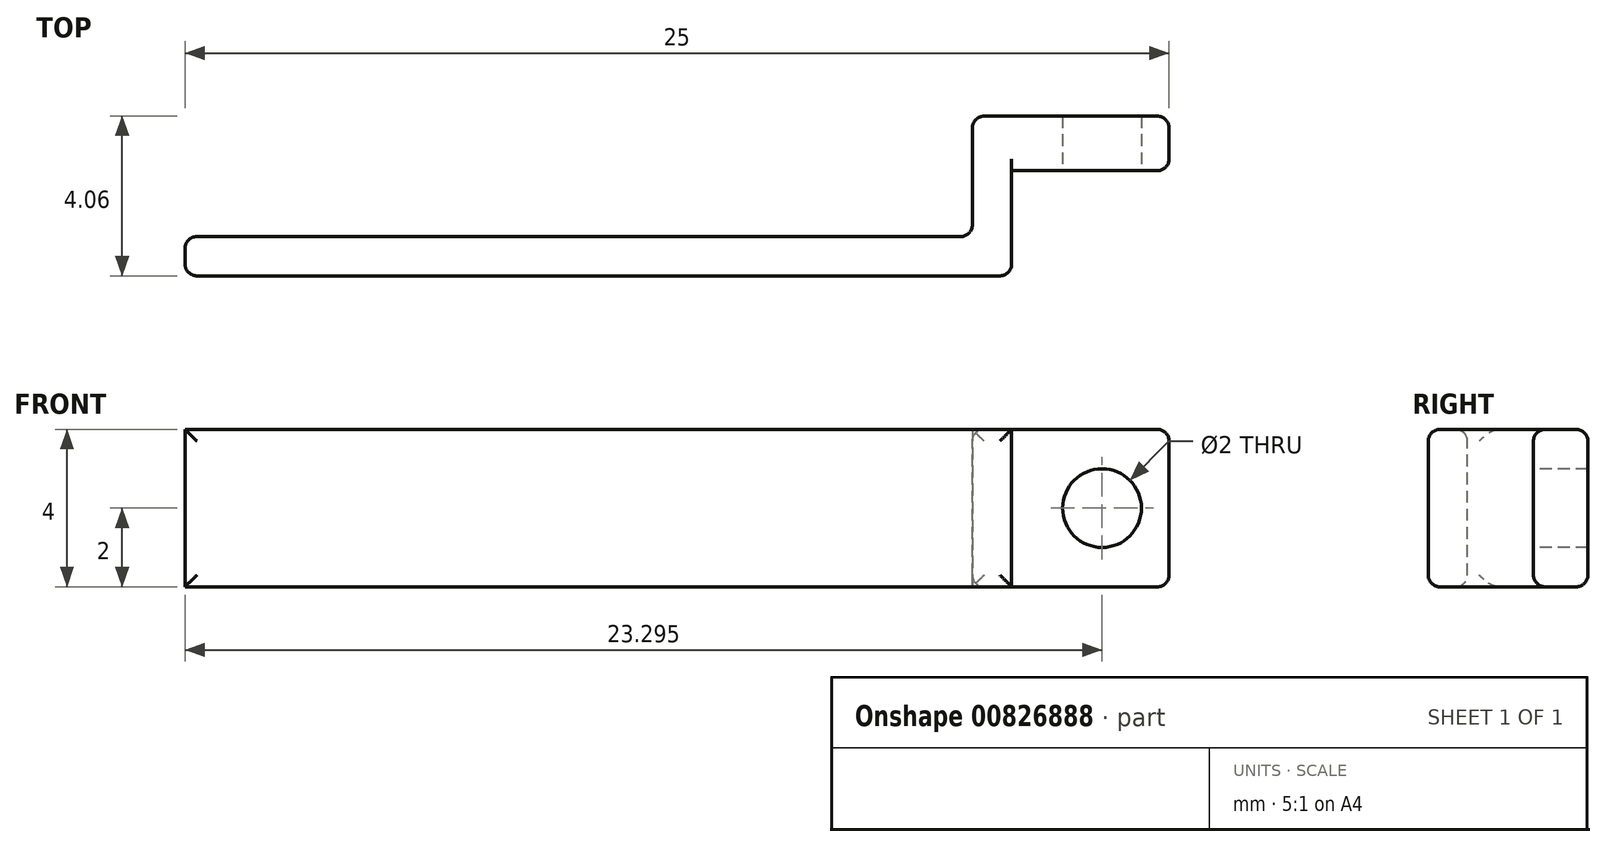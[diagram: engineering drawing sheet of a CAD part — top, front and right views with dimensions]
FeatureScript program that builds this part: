
annotation { "Feature Type Name" : "Feature", "Feature Type Description" : "" }
export const myFeature = defineFeature(function(context is Context, id is Id, definition is map)
    precondition{}
    {
        {
            var Q0;
            Q0=qCreatedBy(makeId("Front.planeOp"),FACE);
            var sketch = newSketch(context, id + "F0", { "sketchPlane" : qUnion([Q0])});
            skLineSegment(sketch, "E0.bottom", {"start": v(0, 0) * mm, "end": v(-20, 0) * mm});
            skLineSegment(sketch, "E0.top", {"start": v(0, 4) * mm, "end": v(-20, 4) * mm});
            skLineSegment(sketch, "E0.left", {"start": v(0, 0) * mm, "end": v(0, 4) * mm});
            skLineSegment(sketch, "E0.right", {"start": v(-20, 0) * mm, "end": v(-20, 4) * mm});
            skSolve(sketch);
        }
        {
            var Q0;
            Q0=makeQuery(id+"F0.imprint","IMPRINT",FACE,{"disambiguationData":[TD([[makeQuery(id+"F0.imprint","IMPRINT",EDGE,{"derivedFrom":sQuery(id+"F0.wireOp",EDGE,"E0.bottom")}),-1.0]])]});
            extrude(context, id + "F1", {"entities" : qUnion([Q0]), "depth" : 1 * mm, "offsetDistance" : 25 * mm});
        }
        {
            var Q0;
            Q0=makeQuery(id+"F1.opExtrude","SWEPT_FACE",FACE,{"disambiguationData":[OSD([sQuery(id+"F0.wireOp",EDGE,"E0.left")])]});
            var sketch = newSketch(context, id + "F2", { "sketchPlane" : qUnion([Q0])});
            skLineSegment(sketch, "E1.bottom", {"start": v(-1, 4) * mm, "end": v(3.06, 4) * mm});
            skLineSegment(sketch, "E1.top", {"start": v(-1, 0) * mm, "end": v(3.06, 0) * mm});
            skLineSegment(sketch, "E1.left", {"start": v(-1, 4) * mm, "end": v(-1, 0) * mm});
            skLineSegment(sketch, "E1.right", {"start": v(3.06, 4) * mm, "end": v(3.06, 0) * mm});
            skSolve(sketch);
        }
        {
            var Q0;
            {var subQ2=sQuery(id+"F2.wireOp",EDGE,"E1.right");Q0=makeQuery(id+"F2.imprint","IMPRINT",FACE,{"disambiguationData":[TD([[makeQuery(id+"F2.imprint","IMPRINT",EDGE,{"derivedFrom":subQ2}),-1.0]])]});}
            var Q1;
            {var subQ2=sQuery(id+"F2.wireOp",EDGE,"E1.left");Q1=makeQuery(id+"F2.imprint","IMPRINT",FACE,{"disambiguationData":[TD([[makeQuery(id+"F2.imprint","IMPRINT",EDGE,{"derivedFrom":subQ2}),-1.0]])]});}
            extrude(context, id + "F3", {"entities" : qUnion([Q0, Q1]), "operationType" : NewBodyOperationType.ADD, "depth" : 1 * mm, "offsetDistance" : 25 * mm});
        }
        {
            var Q0;
            Q0=makeQuery(id+"F3.opExtrude","CAP_FACE",FACE,{"disambiguationData":[OSD([sQuery(id+"F2.wireOp",EDGE,"E1.bottom"),sQuery(id+"F2.wireOp",EDGE,"E1.top"),sQuery(id+"F2.wireOp",EDGE,"E1.left"),sQuery(id+"F2.wireOp",EDGE,"E1.right")])],"isStart":false});
            var sketch = newSketch(context, id + "F4", { "sketchPlane" : qUnion([Q0])});
            skLineSegment(sketch, "E2.bottom", {"start": v(3.06, 4) * mm, "end": v(1.67, 4) * mm});
            skLineSegment(sketch, "E2.top", {"start": v(3.06, 0) * mm, "end": v(1.67, 0) * mm});
            skLineSegment(sketch, "E2.left", {"start": v(3.06, 4) * mm, "end": v(3.06, 0) * mm});
            skLineSegment(sketch, "E2.right", {"start": v(1.67, 4) * mm, "end": v(1.67, 0) * mm});
            skSolve(sketch);
        }
        {
            var Q0;
            Q0=makeQuery(id+"F4.imprint","IMPRINT",FACE,{"disambiguationData":[TD([[makeQuery(id+"F4.imprint","IMPRINT",EDGE,{"derivedFrom":sQuery(id+"F4.wireOp",EDGE,"E2.bottom")}),-1.0]])]});
            extrude(context, id + "F5", {"entities" : qUnion([Q0]), "operationType" : NewBodyOperationType.ADD, "depth" : 4 * mm, "offsetDistance" : 25 * mm});
        }
        {
            var Q0;
            Q0=makeQuery(id+"F5.opExtrude","SWEPT_FACE",FACE,{"disambiguationData":[OSD([sQuery(id+"F4.wireOp",EDGE,"E2.right")])]});
            var sketch = newSketch(context, id + "F6", { "sketchPlane" : qUnion([Q0])});
            skCircle(sketch, "E3", {"center": v(3.3, 2) * mm, "radius": 1 * mm});
            skPoint(sketch, "E3.centerSnap0", {"position": v(1, 2) * mm});
            skSolve(sketch);
        }
        {
            var Q0;
            Q0=makeQuery(id+"F6.imprint","IMPRINT",FACE,{"disambiguationData":[TD([[makeQuery(id+"F6.imprint","IMPRINT",EDGE,{"derivedFrom":sQuery(id+"F6.wireOp",EDGE,"E3")}),1.0]])]});
            extrude(context, id + "F7", {"entities" : qUnion([Q0]), "operationType" : NewBodyOperationType.REMOVE, "oppositeDirection" : true, "depth" : 2 * mm, "offsetDistance" : 25 * mm});
        }
        {
            var Q0;
            Q0=makeQuery(id+"F3.boolean.opBoolean","MERGE",FACE,{"derivedFrom":[makeQuery(id+"F1.opExtrude","CAP_FACE",FACE,{"disambiguationData":[OSD([sQuery(id+"F0.wireOp",EDGE,"E0.bottom"),sQuery(id+"F0.wireOp",EDGE,"E0.top"),sQuery(id+"F0.wireOp",EDGE,"E0.left"),sQuery(id+"F0.wireOp",EDGE,"E0.right")])],"isStart":false}),makeQuery(id+"F3.opExtrude","SWEPT_FACE",FACE,{"disambiguationData":[OSD([sQuery(id+"F2.wireOp",EDGE,"E1.left")])]})]});
            var Q1;
            Q1=makeQuery(id+"F1.opExtrude","CAP_FACE",FACE,{"disambiguationData":[OSD([sQuery(id+"F0.wireOp",EDGE,"E0.bottom"),sQuery(id+"F0.wireOp",EDGE,"E0.top"),sQuery(id+"F0.wireOp",EDGE,"E0.left"),sQuery(id+"F0.wireOp",EDGE,"E0.right")])],"isStart":true});
            var Q2;
            Q2=makeQuery(id+"F5.boolean.opBoolean","MERGE",EDGE,{"derivedFrom":[makeQuery(id+"F3.opExtrude","SWEPT_EDGE",EDGE,{"disambiguationData":[OSD([sQuery(id+"F2.wireOp",EDGE,"E1.top"),sQuery(id+"F2.wireOp",EDGE,"E1.right")])]}),makeQuery(id+"F5.opExtrude","SWEPT_EDGE",EDGE,{"disambiguationData":[OSD([sQuery(id+"F4.wireOp",EDGE,"E2.top"),sQuery(id+"F4.wireOp",EDGE,"E2.left")])]})]});
            var Q3;
            Q3=makeQuery(id+"F5.boolean.opBoolean","MERGE",EDGE,{"derivedFrom":[makeQuery(id+"F3.opExtrude","SWEPT_EDGE",EDGE,{"disambiguationData":[OSD([sQuery(id+"F2.wireOp",EDGE,"E1.bottom"),sQuery(id+"F2.wireOp",EDGE,"E1.right")])]}),makeQuery(id+"F5.opExtrude","SWEPT_EDGE",EDGE,{"disambiguationData":[OSD([sQuery(id+"F4.wireOp",EDGE,"E2.bottom"),sQuery(id+"F4.wireOp",EDGE,"E2.left")])]})]});
            var Q4;
            Q4=makeQuery(id+"F5.opExtrude","CAP_EDGE",EDGE,{"disambiguationData":[OSD([sQuery(id+"F4.wireOp",EDGE,"E2.left")])],"isStart":false});
            var Q5;
            Q5=makeQuery(id+"F3.opExtrude","CAP_EDGE",EDGE,{"disambiguationData":[OSD([sQuery(id+"F2.wireOp",EDGE,"E1.right")])],"isStart":true});
            var Q6;
            Q6=makeQuery(id+"F5.opExtrude","CAP_FACE",FACE,{"disambiguationData":[OSD([sQuery(id+"F4.wireOp",EDGE,"E2.bottom"),sQuery(id+"F4.wireOp",EDGE,"E2.top"),sQuery(id+"F4.wireOp",EDGE,"E2.left"),sQuery(id+"F4.wireOp",EDGE,"E2.right")])],"isStart":false});
            var Q7;
            Q7=makeQuery(id+"F5.opExtrude","SWEPT_EDGE",EDGE,{"disambiguationData":[OSD([sQuery(id+"F2.wireOp",EDGE,"E1.top"),sQuery(id+"F4.wireOp",EDGE,"E2.top"),sQuery(id+"F4.wireOp",EDGE,"E2.right")])]});
            var Q8;
            Q8=makeQuery(id+"F5.opExtrude","SWEPT_EDGE",EDGE,{"disambiguationData":[OSD([sQuery(id+"F2.wireOp",EDGE,"E1.bottom"),sQuery(id+"F4.wireOp",EDGE,"E2.bottom"),sQuery(id+"F4.wireOp",EDGE,"E2.right")])]});
            var Q9;
            Q9=makeQuery(id+"F5.opExtrude","CAP_EDGE",EDGE,{"disambiguationData":[OSD([sQuery(id+"F4.wireOp",EDGE,"E2.right")])],"isStart":true});
            fillet(context, id + "F8", {"entities" : qUnion([Q0, Q1, Q2, Q3, Q4, Q5, Q6, Q7, Q8, Q9]), "radius" : 0.3 * mm, "tangentPropagation" : true, "allowEdgeOverflow" : false});
        }
    });
